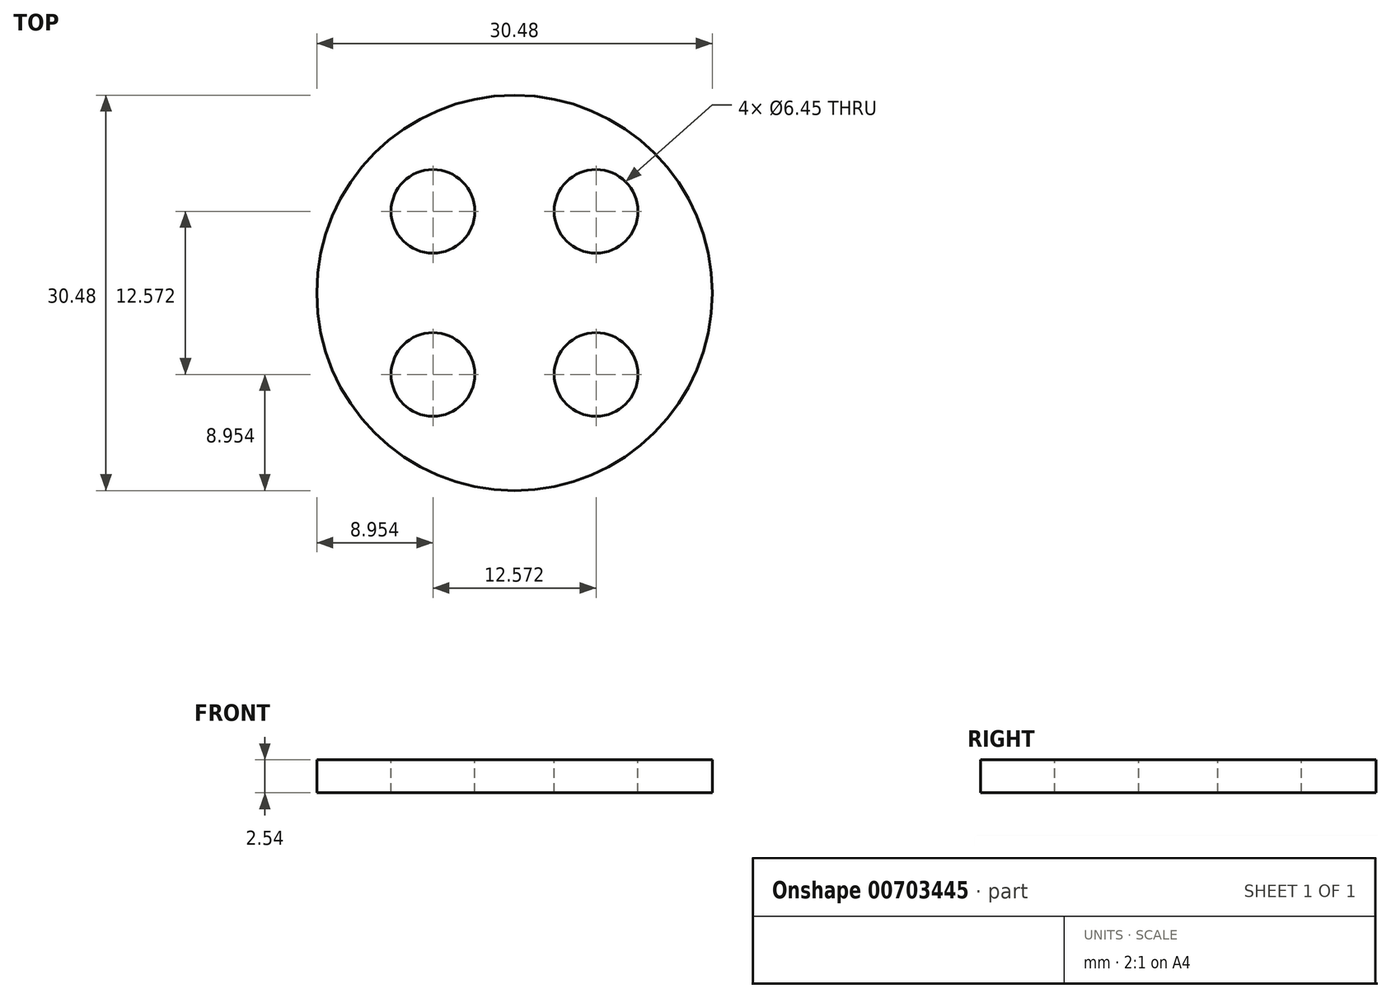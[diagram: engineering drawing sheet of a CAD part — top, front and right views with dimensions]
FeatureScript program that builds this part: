
annotation { "Feature Type Name" : "Feature", "Feature Type Description" : "" }
export const myFeature = defineFeature(function(context is Context, id is Id, definition is map)
    precondition{}
    {
        {
            var Q0;
            Q0=qCreatedBy(makeId("Top.planeOp"),FACE);
            var sketch = newSketch(context, id + "F0", { "sketchPlane" : qUnion([Q0])});
            skCircle(sketch, "E0", {"center": v(0, 0) * mm, "radius": 15.24 * mm});
            skSolve(sketch);
        }
        {
            var Q0;
            Q0=makeQuery(id+"F0.imprint","IMPRINT",FACE,{"disambiguationData":[TD([[makeQuery(id+"F0.imprint","IMPRINT",EDGE,{"derivedFrom":sQuery(id+"F0.wireOp",EDGE,"E0")}),1.0]])]});
            var sketch = newSketch(context, id + "F1", { "sketchPlane" : qUnion([Q0])});
            skCircle(sketch, "E1", {"center": v(6.29, 6.29) * mm, "radius": 3.23 * mm});
            skCircle(sketch, "E2.MirrorC", {"center": v(-6.29, 6.29) * mm, "radius": 3.23 * mm});
            skCircle(sketch, "E3.MirrorC", {"center": v(6.29, -6.29) * mm, "radius": 3.23 * mm});
            skCircle(sketch, "E4.MirrorC", {"center": v(-6.29, -6.29) * mm, "radius": 3.23 * mm});
            skLineSegment(sketch, "E5", {"start": v(0, 18.95) * mm, "end": v(0, -19.2) * mm, "construction": true});
            skLineSegment(sketch, "E6", {"start": v(-20.23, 0) * mm, "end": v(22.64, 0) * mm, "construction": true});
            skLineSegment(sketch, "E7", {"start": v(0, 0) * mm, "end": v(-10.78, 10.78) * mm, "construction": true});
            skPoint(sketch, "E8.middle", {"position": v(0, 0) * mm});
            skSolve(sketch);
        }
        {
            var Q0;
            Q0=qSketchRegion(id+"F0",true);
            extrude(context, id + "F2", {"entities" : qUnion([Q0]), "endBound" : BoundingType.SYMMETRIC, "depth" : 2.54 * mm, "offsetDistance" : 25.4 * mm});
        }
        {
            var Q0;
            Q0=qSketchRegion(id+"F1",true);
            extrude(context, id + "F3", {"entities" : qUnion([Q0]), "operationType" : NewBodyOperationType.REMOVE, "endBound" : BoundingType.SYMMETRIC, "oppositeDirection" : true, "depth" : 2.54 * mm, "offsetDistance" : 25.4 * mm});
        }
    });
